# Revit family: 800х1000
name_source: partatom
category: Обобщенные модели
units: mm (PartAtom-declared; Revit-internal decimal feet)

## family parameters
Всегда вертикально = Да
Может служить основой для арматурных стержней = Нет
На основе рабочей плоскости = Нет
Общий = Нет
При загрузке вырезать с полостями = Нет
Размер круглого соединителя = Использовать диаметр
Тип детали = Нормальный
Точка расчета площади = Нет

## types (12) — shared parameters
ADSK_URL страницы изделия = https://www.ssd.ru
ADSK_Единица измерения = шт
ADSK_Завод-изготовитель = АО СВЯЗЬСТРОЙДЕТАЛЬ
Материал колес и ручек = Металл белый
zero-valued in all types: Ноль

## per-type parameters (varying)
| type | ADSK_Код изделия | ADSK_Масса_Текст | ADSK_Наименование | ADSK_Размер_Высота | Двустворчатая дверь | Материал каркаса | Материал крепежей | Не двустворчатая дверь | Описание |
| ШТ-НП-С-33U-800-1000-ПП-Ч | 130411-01427 | 106.0 | Шкаф телекоммуникационный напольный серверный черный 19&quot;.33U(800x1000) . ШТ-НП-С-33U-800-1000-ПП-Ч передняя.задняя двери перфорированные ССД | 1667 мм | Нет | Металл черный | Металл черный | Да | Шкаф телекоммуникационный напольный серверный черный 19&quot;.33U(800x1000) . ШТ-НП-С-33U-800-1000-ПП-Ч передняя.задняя двери перфорированные ССД |
| ШТ-НП-С-33U-800-1000-П2П-Ч | 130411-01428 | 106.0 | Шкаф телекоммуникационный напольный серверный черный 19&quot;.33U(800x1000) . ШТ-НП-С-33U-800-1000-П2П-Ч передняя перфорипрованная.задняя перф.двойная. ССД | 1667 мм | Да | Металл черный | Металл черный | Нет | Шкаф телекоммуникационный напольный серверный черный 19&quot;.33U(800x1000) . ШТ-НП-С-33U-800-1000-П2П-Ч передняя перфорипрованная.задняя перф.двойная. ССД |
| ШТ-НП-С-42U-800-1000-ПП-Ч | 130411-01429 | 122.0 | Шкаф телекоммуникационный напольный серверный черный 19&quot;.42U(800x1000) . ШТ-НП-С-42U-800-1000-ПП-Ч передняя.задняя двери перфорированные ССД | 2067 мм | Нет | Металл черный | Металл черный | Да | Шкаф телекоммуникационный напольный серверный черный 19&quot;.42U(800x1000) . ШТ-НП-С-42U-800-1000-ПП-Ч передняя.задняя двери перфорированные ССД |
| ШТ-НП-С-42U-800-1000-П2П-Ч | 130411-01430 | 122.0 | Шкаф телекоммуникационный напольный серверный черный 19&quot;.42U(800x1000) . ШТ-НП-С-42U-800-1000-П2П-Ч передняя перфорированная.задняя перф.двойная. ССД | 2067 мм | Да | Металл черный | Металл черный | Нет | Шкаф телекоммуникационный напольный серверный черный 19&quot;.42U(800x1000) . ШТ-НП-С-42U-800-1000-П2П-Ч передняя перфорированная.задняя перф.двойная. ССД |
| ШТ-НП-С-47U-800-1000-ПП-Ч | 130411-01431 | 130.0 | Шкаф телекоммуникационный напольный серверный черный 19&quot;.47U(800x1000) . ШТ-НП-С-47U-800-1000-ПП-Ч передняя.задняя двери перфорированные ССД | 2289 мм | Нет | Металл черный | Металл черный | Да | Шкаф телекоммуникационный напольный серверный черный 19&quot;.47U(800x1000) . ШТ-НП-С-47U-800-1000-ПП-Ч передняя.задняя двери перфорированные ССД |
| ШТ-НП-С-47U-800-1000-П2П-Ч | 130411-01396 | 130.0 | Шкаф телекоммуникационный напольный серверный 19&quot;.47U(800x1000) . ШТ-НП-С-47U-800-1000-П2П-Ч передняя дверь перфор..задняя перф.двойная ССД чер | 2289 мм | Да | Металл черный | Металл черный | Нет | Шкаф телекоммуникационный напольный серверный 19&quot;.47U(800x1000) . ШТ-НП-С-47U-800-1000-П2П-Ч передняя дверь перфор..задняя перф.двойная ССД чер |
| ШТ-НП-С-33U-800-1000-ПП | 130411-00927 | 106.0 | Шкаф телекоммуникационный напольный серверный 19&quot;.33U(800x1000) . ШТ-НП-С-33U-800-1000-ПП передняя.задняя двери перфорированные ССД | 1667 мм | Нет | Металл | Металл | Да | Шкаф телекоммуникационный напольный серверный 19&quot;.33U(800x1000) . ШТ-НП-С-33U-800-1000-ПП передняя.задняя двери перфорированные ССД |
| ШТ-НП-С-33U-800-1000-П2П | 130411-00928 | 106.0 | Шкаф телекоммуникационный напольный серверный 19&quot;.33U(800x1000) . ШТ-НП-С-33U-800-1000-П2П передняя дверь перфорипрованная.задняя перф.двойная. ССД | 1667 мм | Да | Металл | Металл | Нет | Шкаф телекоммуникационный напольный серверный 19&quot;.33U(800x1000) . ШТ-НП-С-33U-800-1000-П2П передняя дверь перфорипрованная.задняя перф.двойная. ССД |
| ШТ-НП-С-42U-800-1000-ПП | 130411-00929 | 122.0 | Шкаф телекоммуникационный напольный серверный 19&quot;.42U(800x1000) . ШТ-НП-С-42U-800-1000-ПП передняя.задняя двери перфорированные ССД | 2067 мм | Нет | Металл | Металл | Да | Шкаф телекоммуникационный напольный серверный 19&quot;.42U(800x1000) . ШТ-НП-С-42U-800-1000-ПП передняя.задняя двери перфорированные ССД |
| ШТ-НП-С-42U-800-1000-П2П | 130411-00930 | 122.0 | Шкаф телекоммуникационный напольный серверный 19&quot;.42U(800x1000) . ШТ-НП-С-42U-800-1000-П2П передняя дверь перфорированная.задняя перф.двойная. ССД | 2067 мм | Да | Металл | Металл | Нет | Шкаф телекоммуникационный напольный серверный 19&quot;.42U(800x1000) . ШТ-НП-С-42U-800-1000-П2П передняя дверь перфорированная.задняя перф.двойная. ССД |
| ШТ-НП-С-47U-800-1000-ПП | 130411-00931 | 130.0 | Шкаф телекоммуникационный напольный серверный 19&quot;.47U(800x1000) . ШТ-НП-С-47U-800-1000-ПП передняя.задняя двери перфорированные ССД | 2289 мм | Нет | Металл | Металл | Да | Шкаф телекоммуникационный напольный серверный 19&quot;.47U(800x1000) . ШТ-НП-С-47U-800-1000-ПП передняя.задняя двери перфорированные ССД |
| ШТ-НП-С-47U-800-1000-П2П | 130411-00932 | 130.0 | Шкаф телекоммуникационный напольный серверный 19&quot;.47U(800x1000) . ШТ-НП-С-47U-800-1000-П2П передняя дверь перфорипрованная.задняя перф.двойная. ССД | 2289 мм | Да | Металл | Металл | Нет | Шкаф телекоммуникационный напольный серверный 19&quot;.47U(800x1000) . ШТ-НП-С-47U-800-1000-П2П передняя дверь перфорипрованная.задняя перф.двойная. ССД |

note: column(s) folded — value = type name in every type: ADSK_Наименование краткое

## geometry (parser evidence)
native form markers: Blend x4
no freeform markers — native parametric forms only
